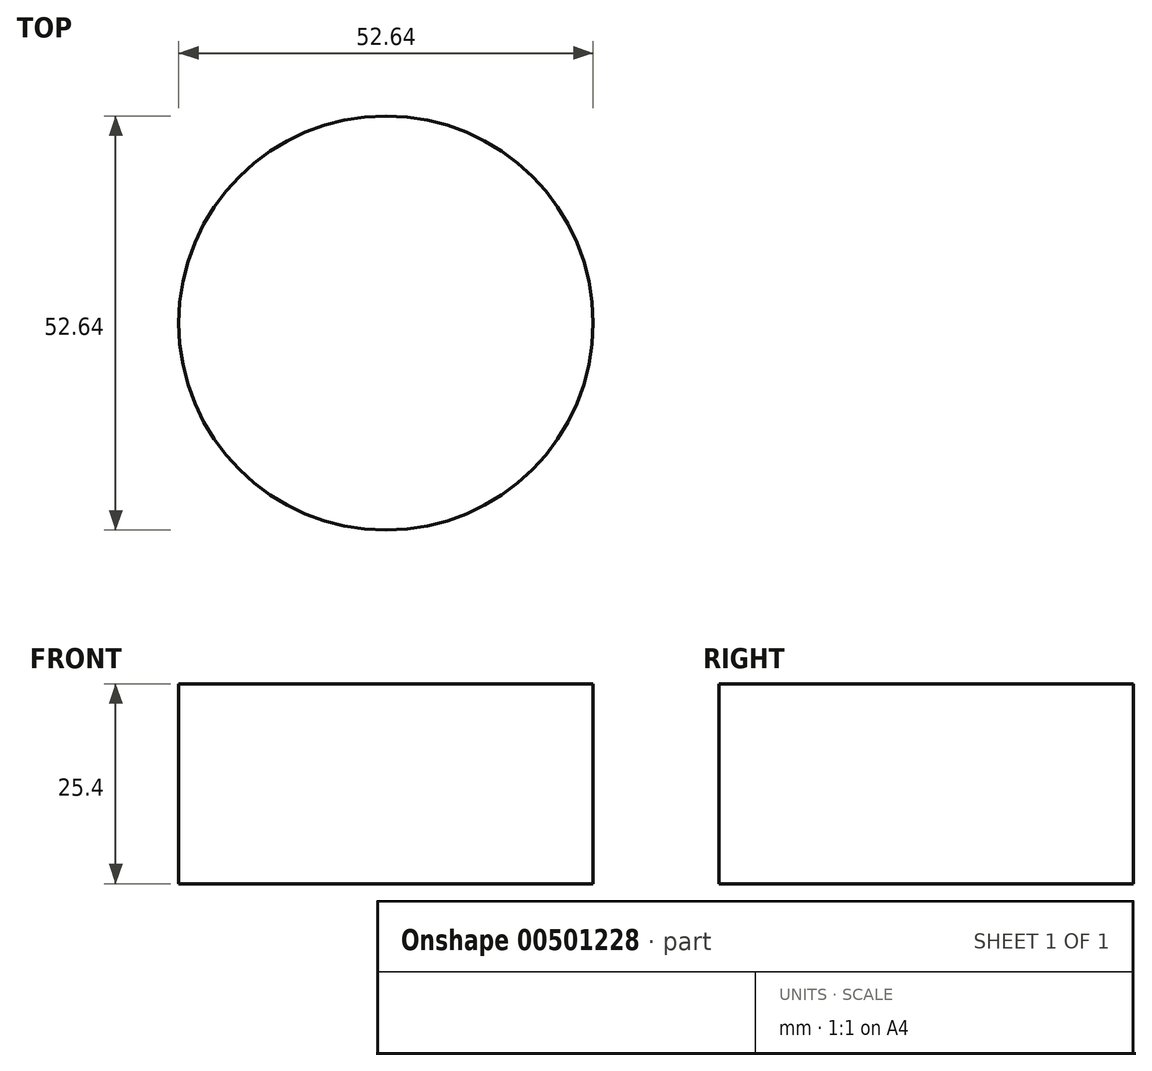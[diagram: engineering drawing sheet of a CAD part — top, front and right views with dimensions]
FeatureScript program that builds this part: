
annotation { "Feature Type Name" : "Feature", "Feature Type Description" : "" }
export const myFeature = defineFeature(function(context is Context, id is Id, definition is map)
    precondition{}
    {
        {
            var Q0;
            Q0=qCreatedBy(makeId("Top.planeOp"),FACE);
            var sketch = newSketch(context, id + "F0", { "sketchPlane" : qUnion([Q0])});
            skCircle(sketch, "E0", {"center": v(0, 0) * mm, "radius": 26.32 * mm});
            skSolve(sketch);
        }
        {
            var Q0;
            Q0 = qSketchRegion(id + "F0", true);
            extrude(context, id + "F1", {"entities" : qUnion([Q0]), "depth" : 25.4 * mm});
        }
    });
